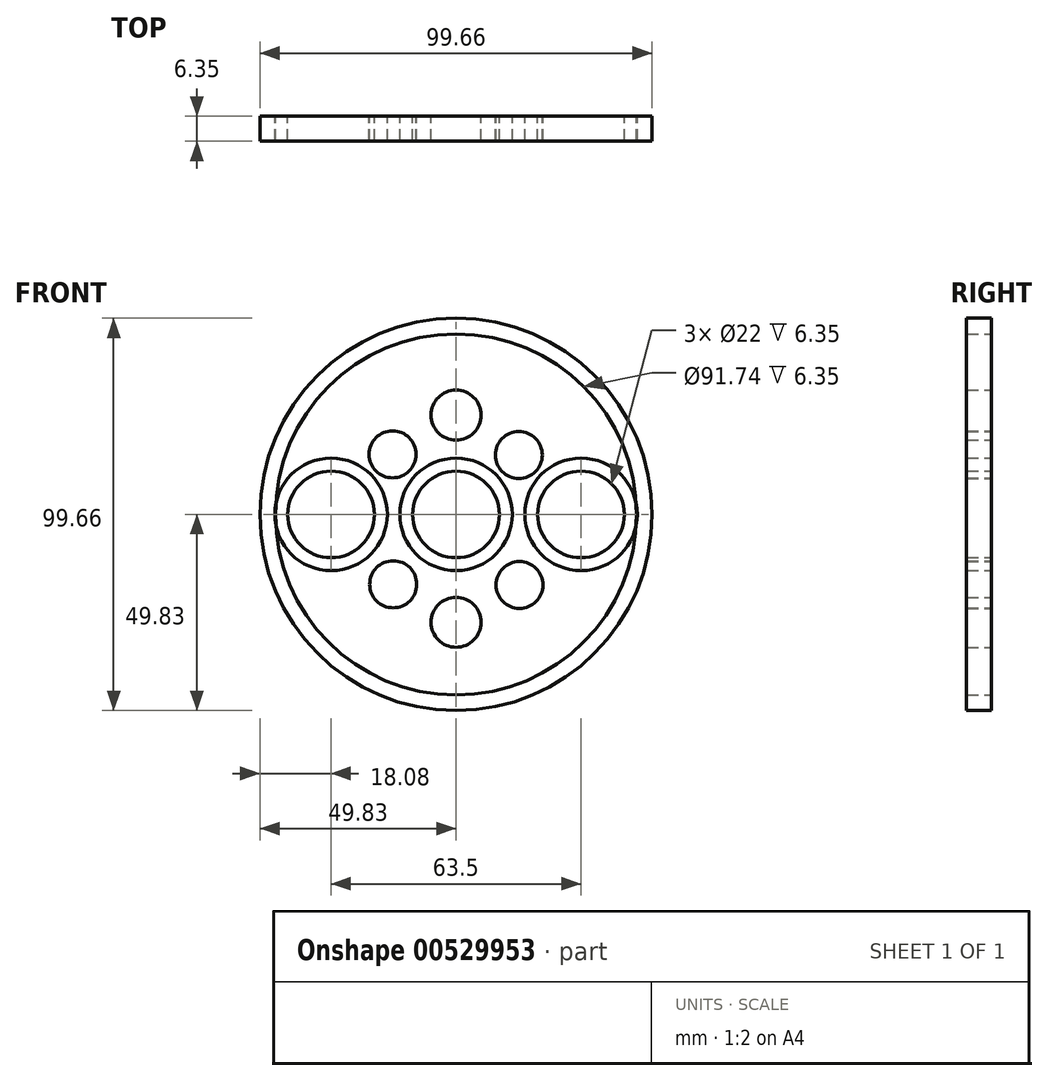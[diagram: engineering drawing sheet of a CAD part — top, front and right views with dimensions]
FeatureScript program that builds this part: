
annotation { "Feature Type Name" : "Feature", "Feature Type Description" : "" }
export const myFeature = defineFeature(function(context is Context, id is Id, definition is map)
    precondition{}
    {
        {
            var Q0;
            Q0=qCreatedBy(makeId("Front.planeOp"),FACE);
            var sketch = newSketch(context, id + "F0", { "sketchPlane" : qUnion([Q0])});
            skCircle(sketch, "E0", {"center": v(0, 0) * mm, "radius": 14.29 * mm});
            skCircle(sketch, "E1", {"center": v(0, 0) * mm, "radius": 11 * mm});
            skCircle(sketch, "E2", {"center": v(-31.75, 0) * mm, "radius": 14.29 * mm});
            skCircle(sketch, "E3", {"center": v(-31.75, 0) * mm, "radius": 11 * mm});
            skPoint(sketch, "E4.center.orphan", {"position": v(33.94, 0) * mm});
            skCircle(sketch, "E5.1.2", {"center": v(31.75, 0) * mm, "radius": 14.29 * mm});
            skCircle(sketch, "E5.1.3", {"center": v(31.75, 0) * mm, "radius": 11 * mm});
            skSolve(sketch);
        }
        {
            var Q0;
            Q0=qCreatedBy(makeId("Front.planeOp"),FACE);
            var sketch = newSketch(context, id + "F1", { "sketchPlane" : qUnion([Q0])});
            skCircle(sketch, "E6", {"center": v(-16.12, 15.25) * mm, "radius": 5.97 * mm});
            skCircle(sketch, "E7", {"center": v(15.94, 15.08) * mm, "radius": 5.97 * mm});
            skCircle(sketch, "E8", {"center": v(-15.96, -17.77) * mm, "radius": 5.97 * mm});
            skCircle(sketch, "E9", {"center": v(16.12, -17.94) * mm, "radius": 5.97 * mm});
            skCircle(sketch, "E10", {"center": v(0, 0) * mm, "radius": 45.87 * mm});
            skCircle(sketch, "E11", {"center": v(0, 0) * mm, "radius": 49.83 * mm});
            skSolve(sketch);
        }
        {
            var Q0;
            Q0=makeQuery(id+"F1.imprint","IMPRINT",FACE,{"disambiguationData":[TD([[makeQuery(id+"F1.imprint","IMPRINT",EDGE,{"derivedFrom":sQuery(id+"F1.wireOp",EDGE,"E10")}),-1.0]])]});
            var sketch = newSketch(context, id + "F2", { "sketchPlane" : qUnion([Q0])});
            skCircle(sketch, "E12.0", {"center": v(-16.12, 15.25) * mm, "radius": 5.97 * mm});
            skCircle(sketch, "E13.0", {"center": v(15.94, 15.08) * mm, "radius": 5.97 * mm});
            skCircle(sketch, "E14.0", {"center": v(16.12, -17.94) * mm, "radius": 5.97 * mm});
            skCircle(sketch, "E15.0", {"center": v(-15.96, -17.77) * mm, "radius": 5.97 * mm});
            skCircle(sketch, "E16.0.0", {"center": v(0, 0) * mm, "radius": 14.29 * mm});
            skCircle(sketch, "E17.0", {"center": v(0, 0) * mm, "radius": 11 * mm});
            skCircle(sketch, "E18.0", {"center": v(31.75, 0) * mm, "radius": 14.29 * mm});
            skCircle(sketch, "E19.0", {"center": v(31.75, 0) * mm, "radius": 11 * mm});
            skCircle(sketch, "E20.0", {"center": v(-31.75, 0) * mm, "radius": 11 * mm});
            skCircle(sketch, "E21.0", {"center": v(-31.75, 0) * mm, "radius": 14.29 * mm});
            skCircle(sketch, "E22.0", {"center": v(0, 0) * mm, "radius": 45.87 * mm});
            skCircle(sketch, "E23.0", {"center": v(0, 0) * mm, "radius": 49.83 * mm});
            skSolve(sketch);
        }
        {
            var Q0;
            Q0=makeQuery(id+"F0.imprint","IMPRINT",FACE,{"disambiguationData":[TD([[makeQuery(id+"F0.imprint","IMPRINT",EDGE,{"derivedFrom":sQuery(id+"F0.wireOp",EDGE,"E0")}),1.0]])]});
            var Q1;
            Q1=makeQuery(id+"F0.imprint","IMPRINT",FACE,{"disambiguationData":[TD([[makeQuery(id+"F0.imprint","IMPRINT",EDGE,{"derivedFrom":sQuery(id+"F0.wireOp",EDGE,"E5.1.2")}),1.0]])]});
            var Q2;
            Q2=makeQuery(id+"F0.imprint","IMPRINT",FACE,{"disambiguationData":[TD([[makeQuery(id+"F0.imprint","IMPRINT",EDGE,{"derivedFrom":sQuery(id+"F0.wireOp",EDGE,"E2")}),1.0]])]});
            var Q3;
            Q3=makeQuery(id+"F1.imprint","IMPRINT",FACE,{"disambiguationData":[TD([[makeQuery(id+"F1.imprint","IMPRINT",EDGE,{"derivedFrom":sQuery(id+"F1.wireOp",EDGE,"E10")}),-1.0]])]});
            extrude(context, id + "F3", {"entities" : qUnion([Q0, Q1, Q2, Q3]), "depth" : 6.35 * mm, "offsetDistance" : 25.4 * mm});
        }
        {
            var Q0;
            Q0=makeQuery(id+"F2.imprint","IMPRINT",FACE,{"disambiguationData":[TD([[makeQuery(id+"F2.imprint","IMPRINT",EDGE,{"derivedFrom":sQuery(id+"F2.wireOp",EDGE,"E12.0")}),-1.0]])]});
            var sketch = newSketch(context, id + "F4", { "sketchPlane" : qUnion([Q0])});
            skCircle(sketch, "E24", {"center": v(0, 25.22) * mm, "radius": 9.07 * mm});
            skCircle(sketch, "E25", {"center": v(0, -27.4) * mm, "radius": 9.08 * mm});
            skCircle(sketch, "E26", {"center": v(0, 25.22) * mm, "radius": 6.35 * mm});
            skCircle(sketch, "E27", {"center": v(0, -27.4) * mm, "radius": 6.35 * mm});
            skSolve(sketch);
        }
        {
            var Q0;
            Q0=qCreatedBy(makeId("Front.planeOp"),FACE);
            var sketch = newSketch(context, id + "F5", { "sketchPlane" : qUnion([Q0])});
            skCircle(sketch, "E28.0", {"center": v(0, 25.22) * mm, "radius": 6.35 * mm});
            skCircle(sketch, "E29.0", {"center": v(0, 25.22) * mm, "radius": 9.07 * mm});
            skCircle(sketch, "E30.0", {"center": v(15.94, 15.08) * mm, "radius": 5.97 * mm});
            skCircle(sketch, "E31.0", {"center": v(16.12, -17.94) * mm, "radius": 5.97 * mm});
            skCircle(sketch, "E32.0", {"center": v(0, -27.4) * mm, "radius": 9.08 * mm});
            skCircle(sketch, "E33.0", {"center": v(0, -27.4) * mm, "radius": 6.35 * mm});
            skCircle(sketch, "E34.0", {"center": v(-15.96, -17.77) * mm, "radius": 5.97 * mm});
            skCircle(sketch, "E35.0", {"center": v(-16.12, 15.25) * mm, "radius": 5.97 * mm});
            skSolve(sketch);
        }
        {
            var Q0;
            Q0=makeQuery(id+"F2.imprint","IMPRINT",FACE,{"disambiguationData":[TD([[makeQuery(id+"F2.imprint","IMPRINT",EDGE,{"derivedFrom":sQuery(id+"F2.wireOp",EDGE,"E13.0")}),1.0]])]});
            var Q1;
            Q1=makeQuery(id+"F2.imprint","IMPRINT",FACE,{"disambiguationData":[TD([[makeQuery(id+"F2.imprint","IMPRINT",EDGE,{"derivedFrom":sQuery(id+"F2.wireOp",EDGE,"E12.0")}),1.0]])]});
            var Q2;
            Q2=makeQuery(id+"F2.imprint","IMPRINT",FACE,{"disambiguationData":[TD([[makeQuery(id+"F2.imprint","IMPRINT",EDGE,{"derivedFrom":sQuery(id+"F2.wireOp",EDGE,"E15.0")}),1.0]])]});
            var Q3;
            Q3=makeQuery(id+"F2.imprint","IMPRINT",FACE,{"disambiguationData":[TD([[makeQuery(id+"F2.imprint","IMPRINT",EDGE,{"derivedFrom":sQuery(id+"F2.wireOp",EDGE,"E14.0")}),1.0]])]});
            var Q4;
            Q4=makeQuery(id+"F4.imprint","IMPRINT",FACE,{"disambiguationData":[TD([[makeQuery(id+"F4.imprint","IMPRINT",EDGE,{"derivedFrom":sQuery(id+"F4.wireOp",EDGE,"E26")}),1.0]])]});
            var Q5;
            Q5=makeQuery(id+"F4.imprint","IMPRINT",FACE,{"disambiguationData":[TD([[makeQuery(id+"F4.imprint","IMPRINT",EDGE,{"derivedFrom":sQuery(id+"F4.wireOp",EDGE,"E27")}),1.0]])]});
            var Q6;
            Q6=sQuery(id+"F5.wireOp",EDGE,"E29.0");
            var Q7;
            Q7=sQuery(id+"F5.wireOp",EDGE,"E28.0");
            var Q8;
            Q8=sQuery(id+"F5.wireOp",EDGE,"E30.0");
            var Q9;
            Q9=sQuery(id+"F5.wireOp",EDGE,"E31.0");
            var Q10;
            Q10=sQuery(id+"F5.wireOp",EDGE,"E32.0");
            var Q11;
            Q11=sQuery(id+"F5.wireOp",EDGE,"E33.0");
            var Q12;
            Q12=sQuery(id+"F5.wireOp",EDGE,"E34.0");
            var Q13;
            Q13=sQuery(id+"F5.wireOp",EDGE,"E35.0");
            extrude(context, id + "F6", {"entities" : qUnion([Q0, Q1, Q2, Q3, Q4, Q5]), "surfaceEntities" : qUnion([Q6, Q7, Q8, Q9, Q10, Q11, Q12, Q13]), "depth" : 6.35 * mm, "offsetDistance" : 25.4 * mm});
        }
    });
